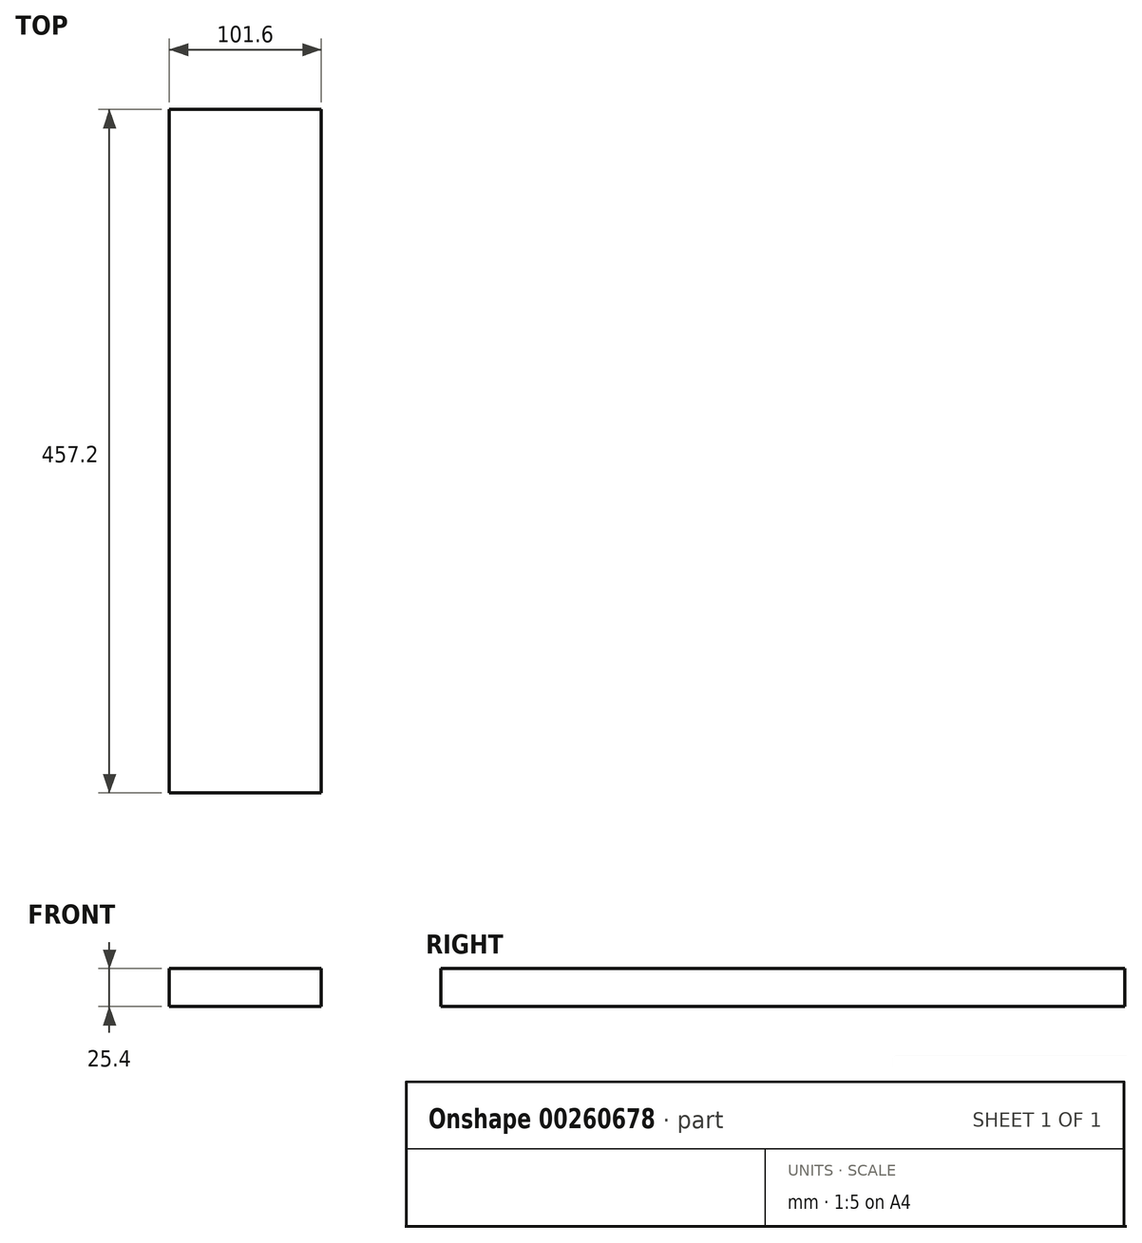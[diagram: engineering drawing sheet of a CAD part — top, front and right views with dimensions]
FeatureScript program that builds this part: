
annotation { "Feature Type Name" : "Feature", "Feature Type Description" : "" }
export const myFeature = defineFeature(function(context is Context, id is Id, definition is map)
    precondition{}
    {
        {
            var Q0;
            Q0=qCreatedBy(makeId("Front.planeOp"),FACE);
            var sketch = newSketch(context, id + "F0", { "sketchPlane" : qUnion([Q0])});
            skLineSegment(sketch, "E0", {"start": v(-42.99, 31.85) * mm, "end": v(-42.99, 6.45) * mm});
            skLineSegment(sketch, "E1", {"start": v(-42.99, 6.45) * mm, "end": v(58.61, 6.45) * mm});
            skLineSegment(sketch, "E2", {"start": v(58.61, 6.45) * mm, "end": v(58.61, 31.85) * mm});
            skLineSegment(sketch, "E3", {"start": v(58.61, 31.85) * mm, "end": v(-42.99, 31.85) * mm});
            skSolve(sketch);
        }
        {
            var Q0;
            Q0=makeQuery(id+"F0.imprint","IMPRINT",FACE,{"disambiguationData":[TD([[makeQuery(id+"F0.imprint","IMPRINT",EDGE,{"derivedFrom":sQuery(id+"F0.wireOp",EDGE,"E0")}),1.0]])]});
            extrude(context, id + "F1", {"entities" : qUnion([Q0]), "depth" : 457.2 * mm});
        }
    });
